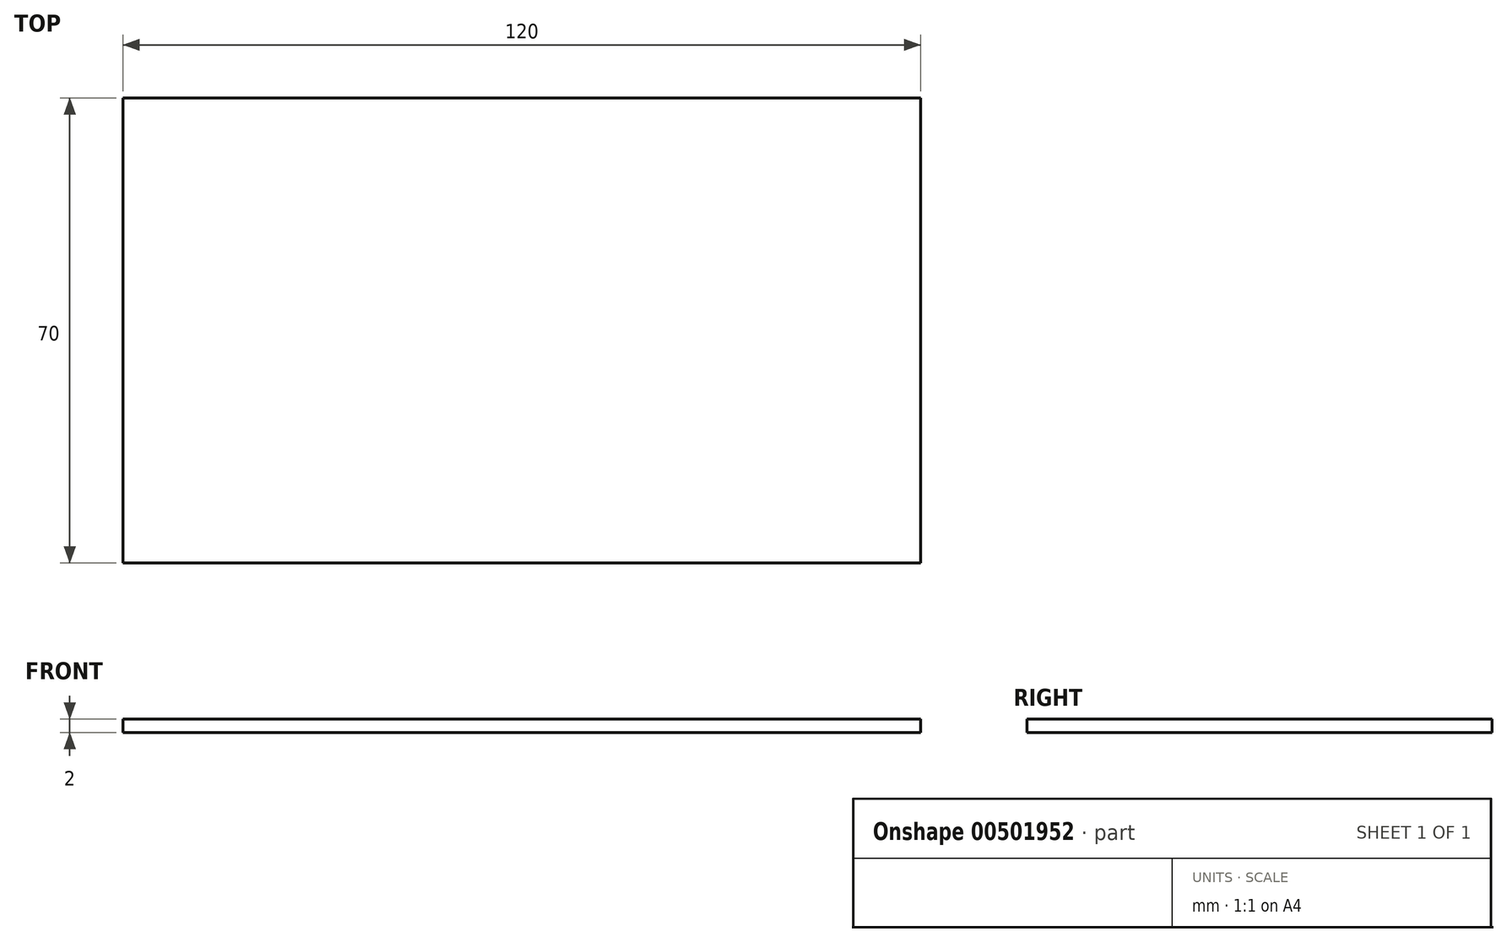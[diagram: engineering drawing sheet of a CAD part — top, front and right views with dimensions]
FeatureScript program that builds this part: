
annotation { "Feature Type Name" : "Feature", "Feature Type Description" : "" }
export const myFeature = defineFeature(function(context is Context, id is Id, definition is map)
    precondition{}
    {
        {
            var Q0;
            Q0=qCreatedBy(makeId("Top.planeOp"),FACE);
            var sketch = newSketch(context, id + "F0", { "sketchPlane" : qUnion([Q0])});
            skLineSegment(sketch, "E0.bottom", {"start": v(60, -35) * mm, "end": v(-60, -35) * mm});
            skLineSegment(sketch, "E0.top", {"start": v(60, 35) * mm, "end": v(-60, 35) * mm});
            skLineSegment(sketch, "E0.left", {"start": v(60, -35) * mm, "end": v(60, 35) * mm});
            skLineSegment(sketch, "E0.right", {"start": v(-60, -35) * mm, "end": v(-60, 35) * mm});
            skPoint(sketch, "E0.middle", {"position": v(0, 0) * mm});
            skSolve(sketch);
        }
        {
            var Q0;
            Q0=makeQuery(id+"F0.imprint","IMPRINT",FACE,{"disambiguationData":[TD([[makeQuery(id+"F0.imprint","IMPRINT",EDGE,{"derivedFrom":sQuery(id+"F0.wireOp",EDGE,"E0.bottom")}),-1.0]])]});
            extrude(context, id + "F1", {"entities" : qUnion([Q0]), "depth" : 2 * mm, "symmetric" : true});
        }
    });
